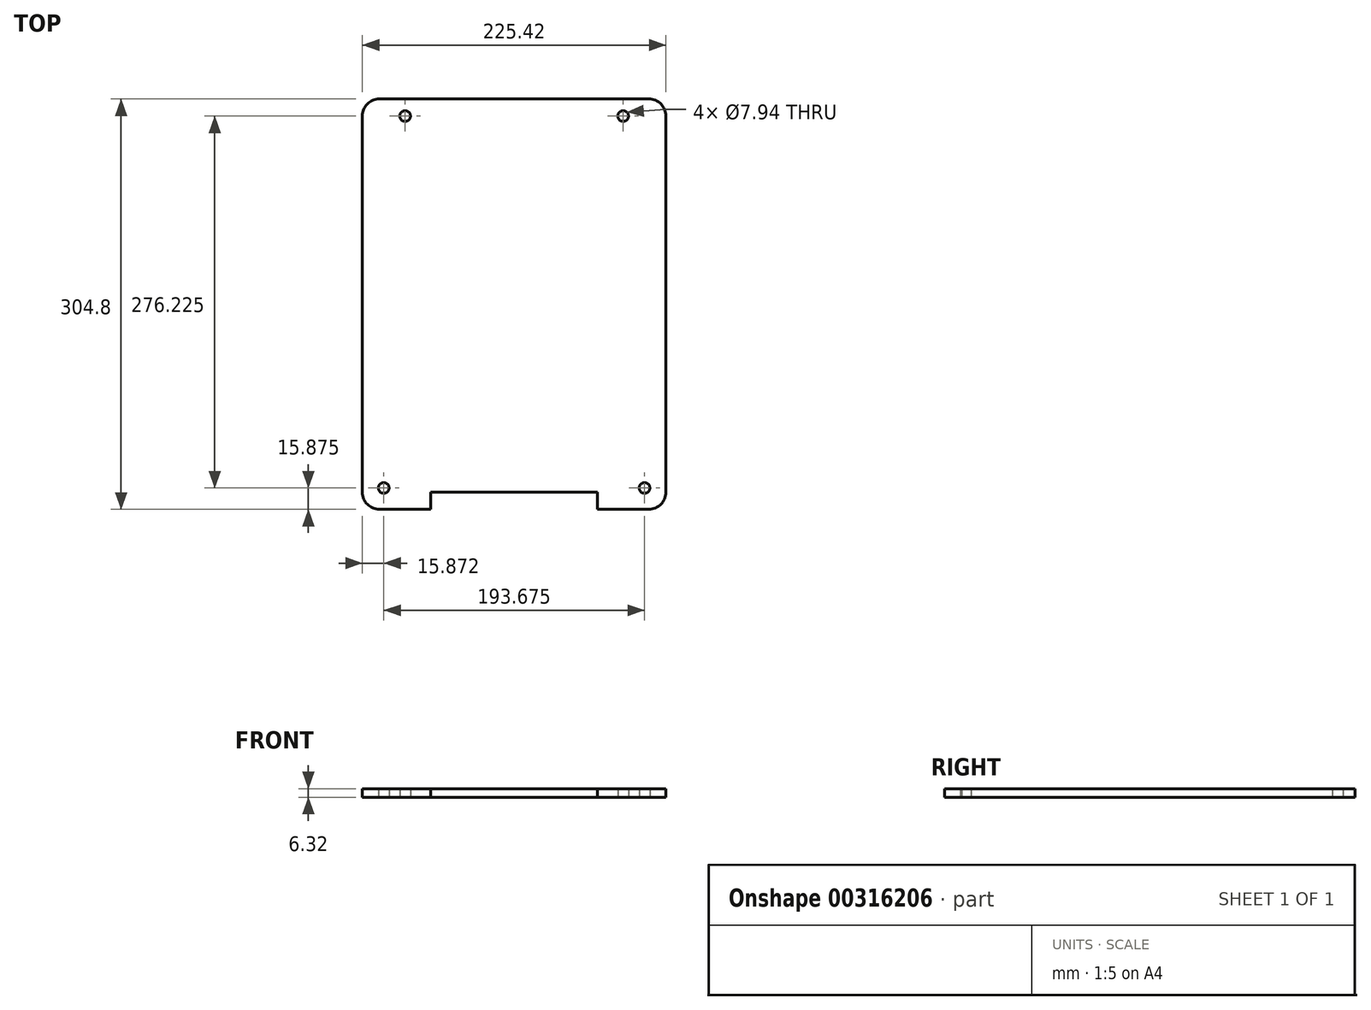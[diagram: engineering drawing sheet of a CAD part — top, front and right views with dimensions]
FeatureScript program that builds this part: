
annotation { "Feature Type Name" : "Feature", "Feature Type Description" : "" }
export const myFeature = defineFeature(function(context is Context, id is Id, definition is map)
    precondition{}
    {
        {
            var Q0;
            Q0=qCreatedBy(makeId("Top.planeOp"),FACE);
            var sketch = newSketch(context, id + "F0", { "sketchPlane" : qUnion([Q0])});
            skLineSegment(sketch, "E0.bottom", {"start": v(100.01, -152.4) * mm, "end": v(61.91, -152.4) * mm});
            skLineSegment(sketch, "E0.top", {"start": v(100.01, 152.4) * mm, "end": v(-100.01, 152.4) * mm});
            skLineSegment(sketch, "E0.left", {"start": v(112.71, -139.7) * mm, "end": v(112.71, 139.7) * mm});
            skLineSegment(sketch, "E0.right", {"start": v(-112.71, -139.7) * mm, "end": v(-112.71, 139.7) * mm});
            skPoint(sketch, "E0.middle", {"position": v(0, 0) * mm});
            skPoint(sketch, "E1.visualSharp", {"position": v(-112.71, 152.4) * mm});
            skArc(sketch, "E1.filletArc", {"start": v(-100.01, 152.4) * mm, "mid": v(-109, 148.68) * mm, "end": v(-112.71, 139.7) * mm});
            skPoint(sketch, "E2.visualSharp", {"position": v(112.71, 152.4) * mm});
            skArc(sketch, "E2.filletArc", {"start": v(112.71, 139.7) * mm, "mid": v(109, 148.68) * mm, "end": v(100.01, 152.4) * mm});
            skPoint(sketch, "E3.visualSharp", {"position": v(-112.71, -152.4) * mm});
            skArc(sketch, "E3.filletArc", {"start": v(-112.71, -139.7) * mm, "mid": v(-109, -148.68) * mm, "end": v(-100.01, -152.4) * mm});
            skPoint(sketch, "E4.visualSharp", {"position": v(112.71, -152.4) * mm});
            skArc(sketch, "E4.filletArc", {"start": v(100.01, -152.4) * mm, "mid": v(109, -148.68) * mm, "end": v(112.71, -139.7) * mm});
            skCircle(sketch, "E5", {"center": v(-96.84, -136.53) * mm, "radius": 3.97 * mm});
            skCircle(sketch, "E6.MirrorC", {"center": v(96.84, -136.53) * mm, "radius": 3.97 * mm});
            skCircle(sketch, "E7", {"center": v(-80.96, 139.7) * mm, "radius": 3.97 * mm});
            skCircle(sketch, "E8.MirrorC", {"center": v(80.96, 139.7) * mm, "radius": 3.97 * mm});
            skLineSegment(sketch, "E9", {"start": v(-61.91, -152.4) * mm, "end": v(-61.91, -139.7) * mm});
            skLineSegment(sketch, "E10", {"start": v(-61.91, -139.7) * mm, "end": v(61.91, -139.7) * mm});
            skLineSegment(sketch, "E11", {"start": v(61.91, -139.7) * mm, "end": v(61.91, -152.4) * mm});
            skLineSegment(sketch, "E12.trimOffspring", {"start": v(-61.91, -152.4) * mm, "end": v(-100.01, -152.4) * mm});
            skSolve(sketch);
        }
        {
            var Q0;
            Q0=makeQuery(id+"F0.imprint","IMPRINT",FACE,{"disambiguationData":[TD([[makeQuery(id+"F0.imprint","IMPRINT",EDGE,{"derivedFrom":sQuery(id+"F0.wireOp",EDGE,"E0.bottom")}),-1.0]])]});
            extrude(context, id + "F1", {"entities" : qUnion([Q0]), "depth" : 6.32 * mm});
        }
    });
